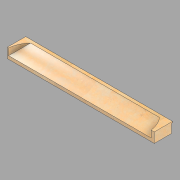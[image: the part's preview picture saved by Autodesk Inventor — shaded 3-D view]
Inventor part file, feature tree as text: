
AUTODESK INVENTOR PART (.ipt)
format: ipt  version: 2022.2 (Build 262287010, 287A)  size: 134,144 bytes
history: native  units: in
note: dims shown in document units (in); Inventor stores cm internally (conversion verified against a paired STEP export)
features: revolve x2, other x1, direct_edit x1
ambient origin geometry x8: Origin, YZ Plane, XZ Plane, XY Plane, X Axis, Y Axis, Z Axis, Center Point
bodies: Solid1 (feature_tree)
feature tree (4):
  other  "Head (L)"
  direct_edit  "Direct Edit1"
  revolve  "Rotate1"  [1 undecoded]
  revolve  "Rotate2"  [1 undecoded]
note: 2 required parameter values undecoded (feature->parameter linkage not recoverable at this tier; creation-order binding heuristic only, values carry confidence <= 0.55)
